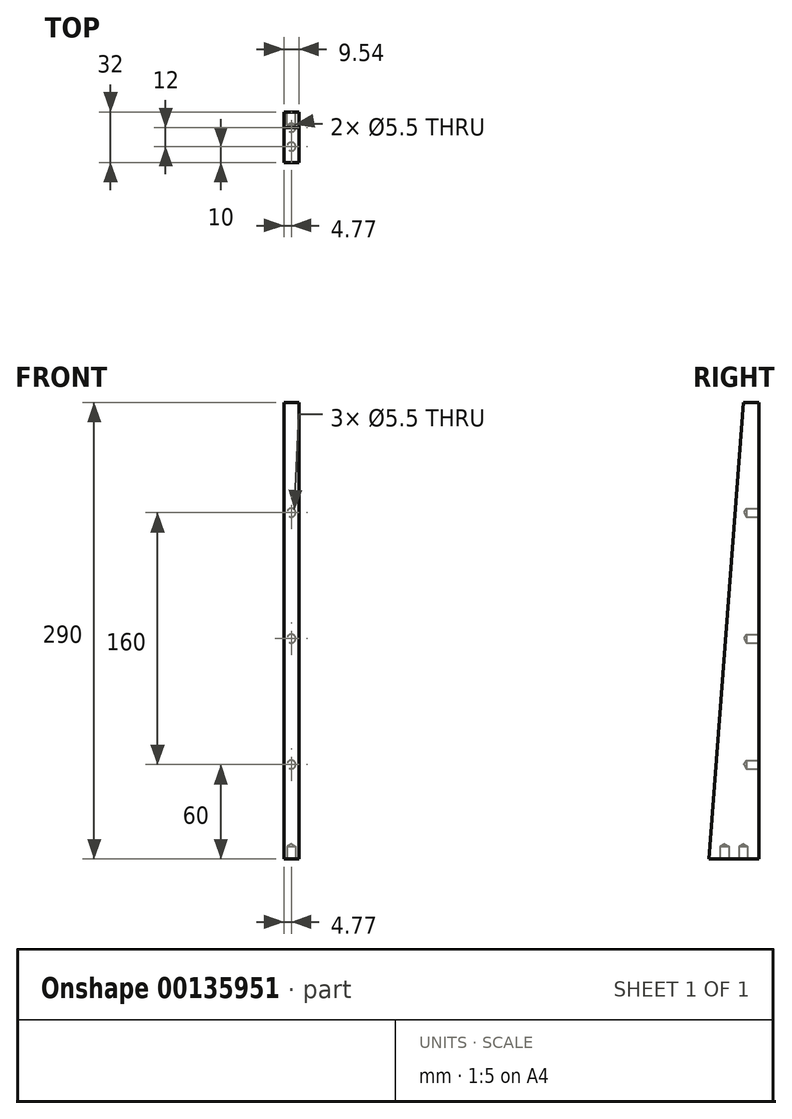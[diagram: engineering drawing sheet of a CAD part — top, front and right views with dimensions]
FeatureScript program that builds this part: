
annotation { "Feature Type Name" : "Feature", "Feature Type Description" : "" }
export const myFeature = defineFeature(function(context is Context, id is Id, definition is map)
    precondition{}
    {
        {
            var Q0;
            Q0=qCreatedBy(makeId("Right.planeOp"),FACE);
            var sketch = newSketch(context, id + "F0", { "sketchPlane" : qUnion([Q0])});
            skLineSegment(sketch, "E0", {"start": v(0, 0) * mm, "end": v(-32, 0) * mm});
            skLineSegment(sketch, "E1", {"start": v(0, 290) * mm, "end": v(0, 0) * mm});
            skLineSegment(sketch, "E2", {"start": v(0, 290) * mm, "end": v(-10, 290) * mm});
            skLineSegment(sketch, "E3", {"start": v(-10, 290) * mm, "end": v(-32, 0) * mm});
            skSolve(sketch);
        }
        {
            var Q0;
            Q0 = qSketchRegion(id + "F0", true);
            extrude(context, id + "F1", {"entities" : qUnion([Q0]), "endBound" : BoundingType.SYMMETRIC, "depth" : 9.53 * mm});
        }
        {
            var Q0;
            Q0=makeQuery(id+"F1.opExtrude","SWEPT_FACE",FACE,{"disambiguationData":[OSD([sQuery(id+"F0.wireOp",EDGE,"E1")])]});
            var sketch = newSketch(context, id + "F2", { "sketchPlane" : qUnion([Q0])});
            skCircle(sketch, "E4", {"center": v(0, 60) * mm, "radius": 2 * mm});
            skCircle(sketch, "E5.0.1.0", {"center": v(0, 140) * mm, "radius": 2 * mm});
            skCircle(sketch, "E5.0.2.0", {"center": v(0, 220) * mm, "radius": 2 * mm});
            skLineSegment(sketch, "E5.direction1", {"start": v(0, 60) * mm, "end": v(25, 60) * mm, "construction": true});
            skLineSegment(sketch, "E5.direction2", {"start": v(0, 60) * mm, "end": v(0, 140) * mm, "construction": true});
            skSolve(sketch);
        }
        {
            var Q0;
            Q0=makeQuery(id+"F1.opExtrude","SWEPT_FACE",FACE,{"disambiguationData":[OSD([sQuery(id+"F0.wireOp",EDGE,"E0")])]});
            var sketch = newSketch(context, id + "F3", { "sketchPlane" : qUnion([Q0])});
            skCircle(sketch, "E6", {"center": v(0, 10) * mm, "radius": 2 * mm});
            skCircle(sketch, "E7", {"center": v(0, 22) * mm, "radius": 2 * mm});
            skSolve(sketch);
        }
        {
            var Q0;
            Q0=sQuery(id+"F2.wireOp",VERTEX,"E4.center");
            var Q1;
            Q1=sQuery(id+"F2.wireOp",VERTEX,"E5.0.1.0.center");
            var Q2;
            Q2=sQuery(id+"F2.wireOp",VERTEX,"E5.0.2.0.center");
            var Q3;
            Q3=sQuery(id+"F3.wireOp",VERTEX,"E7.center");
            var Q4;
            Q4=sQuery(id+"F3.wireOp",VERTEX,"E6.center");
            var Q5;
            Q5=makeQuery(id+"F1.opExtrude","SWEPT_BODY",BODY,{"disambiguationData":[OSD([sQuery(id+"F0.wireOp",EDGE,"E0"),sQuery(id+"F0.wireOp",EDGE,"Z4iyRvXh-uPHR-ABCQ-6QHt-GtgkJ2zhc1f4"),sQuery(id+"F0.wireOp",EDGE,"E1")])]});
            hole(context, id + "F4", {"style" : HoleStyle.SIMPLE, "endStyle" : HoleEndStyle.BLIND, "standardTappedOrClearance" : lookupTablePath({ "standard" : "ISO", "fit" : "Normal", "size" : "M5", "type" : "Clearance" }), "standardBlindInLast" : lookupTablePath({ "fit" : "Standard", "standard" : "ISO", "size" : "M5", "type" : "Clearance" }), "holeDiameter" : 5.5 * mm, "holeDepth" : 8 * mm, "locations" : qUnion([Q0, Q1, Q2, Q3, Q4]), "scope" : qUnion([Q5])});
        }
    });
